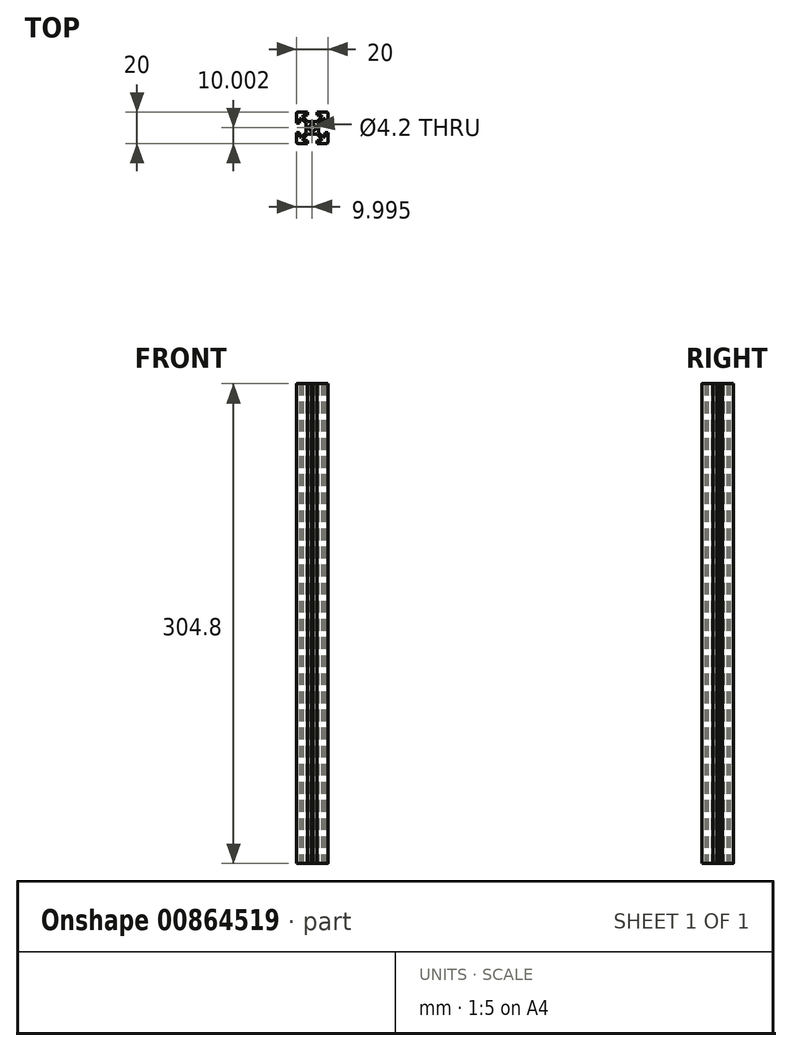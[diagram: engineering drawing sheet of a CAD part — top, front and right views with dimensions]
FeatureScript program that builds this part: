
annotation { "Feature Type Name" : "Feature", "Feature Type Description" : "" }
export const myFeature = defineFeature(function(context is Context, id is Id, definition is map)
    precondition{}
    {
        {
            var Q0;
            Q0=qCreatedBy(makeId("Top.planeOp"),FACE);
            var sketch = newSketch(context, id + "F0", { "sketchPlane" : qUnion([Q0])});
            skLineSegment(sketch, "E0", {"start": v(-2.2, 0) * mm, "end": v(2.2, 0) * mm});
            skLineSegment(sketch, "E1", {"start": v(0, -2.21) * mm, "end": v(0, 2.2) * mm});
            skLineSegment(sketch, "E2", {"start": v(-8, -3) * mm, "end": v(-10, -3) * mm});
            skLineSegment(sketch, "E3", {"start": v(-10, -3) * mm, "end": v(-10, -9) * mm});
            skArc(sketch, "E4", {"start": v(-10, -9) * mm, "mid": v(-9.71, -9.71) * mm, "end": v(-9, -10) * mm});
            skLineSegment(sketch, "E5", {"start": v(-9, -10) * mm, "end": v(-3, -10) * mm});
            skLineSegment(sketch, "E6", {"start": v(-3, -10) * mm, "end": v(-3, -8) * mm});
            skLineSegment(sketch, "E7", {"start": v(-3, -8) * mm, "end": v(-6, -8) * mm});
            skLineSegment(sketch, "E8", {"start": v(-6, -8) * mm, "end": v(-6, -7.07) * mm});
            skLineSegment(sketch, "E9", {"start": v(-6, -7.07) * mm, "end": v(-2.94, -4) * mm});
            skLineSegment(sketch, "E10", {"start": v(-2.94, -4) * mm, "end": v(-0.52, -4) * mm});
            skLineSegment(sketch, "E11", {"start": v(-0.52, -4) * mm, "end": v(0, -3.7) * mm});
            skLineSegment(sketch, "E12", {"start": v(0, -3.7) * mm, "end": v(0.51, -4) * mm});
            skLineSegment(sketch, "E13", {"start": v(0.51, -4) * mm, "end": v(2.93, -4) * mm});
            skLineSegment(sketch, "E14", {"start": v(2.93, -4) * mm, "end": v(6, -7.07) * mm});
            skLineSegment(sketch, "E15", {"start": v(6, -7.07) * mm, "end": v(6, -8) * mm});
            skLineSegment(sketch, "E16", {"start": v(6, -8) * mm, "end": v(3, -8) * mm});
            skLineSegment(sketch, "E17", {"start": v(3, -8) * mm, "end": v(3, -10) * mm});
            skLineSegment(sketch, "E18", {"start": v(3, -10) * mm, "end": v(9, -10) * mm});
            skArc(sketch, "E19", {"start": v(9, -10) * mm, "mid": v(9.7, -9.71) * mm, "end": v(10, -9) * mm});
            skLineSegment(sketch, "E20", {"start": v(10, -9) * mm, "end": v(10, -3) * mm});
            skLineSegment(sketch, "E21", {"start": v(10, -3) * mm, "end": v(8, -3) * mm});
            skLineSegment(sketch, "E22", {"start": v(8, -3) * mm, "end": v(8, -6) * mm});
            skLineSegment(sketch, "E23", {"start": v(8, -6) * mm, "end": v(7.06, -6) * mm});
            skLineSegment(sketch, "E24", {"start": v(7.06, -6) * mm, "end": v(4, -2.95) * mm});
            skLineSegment(sketch, "E25", {"start": v(4, -2.95) * mm, "end": v(4, -0.53) * mm});
            skLineSegment(sketch, "E26", {"start": v(4, -0.53) * mm, "end": v(3.7, 0) * mm});
            skLineSegment(sketch, "E27", {"start": v(3.7, 0) * mm, "end": v(4, 0.51) * mm});
            skLineSegment(sketch, "E28", {"start": v(4, 0.51) * mm, "end": v(4, 2.93) * mm});
            skLineSegment(sketch, "E29", {"start": v(4, 2.93) * mm, "end": v(7.06, 6) * mm});
            skLineSegment(sketch, "E30", {"start": v(7.06, 6) * mm, "end": v(8, 6) * mm});
            skLineSegment(sketch, "E31", {"start": v(8, 6) * mm, "end": v(8, 3) * mm});
            skLineSegment(sketch, "E32", {"start": v(8, 3) * mm, "end": v(10, 3) * mm});
            skLineSegment(sketch, "E33", {"start": v(10, 3) * mm, "end": v(10, 9) * mm});
            skArc(sketch, "E34", {"start": v(10, 9) * mm, "mid": v(9.7, 9.7) * mm, "end": v(9, 10) * mm});
            skLineSegment(sketch, "E35", {"start": v(9, 10) * mm, "end": v(3, 10) * mm});
            skLineSegment(sketch, "E36", {"start": v(3, 10) * mm, "end": v(3, 8) * mm});
            skLineSegment(sketch, "E37", {"start": v(3, 8) * mm, "end": v(6, 8) * mm});
            skLineSegment(sketch, "E38", {"start": v(6, 8) * mm, "end": v(6, 7.05) * mm});
            skLineSegment(sketch, "E39", {"start": v(6, 7.05) * mm, "end": v(2.93, 4) * mm});
            skLineSegment(sketch, "E40", {"start": v(2.93, 4) * mm, "end": v(0.51, 4) * mm});
            skLineSegment(sketch, "E41", {"start": v(0.51, 4) * mm, "end": v(0, 3.7) * mm});
            skLineSegment(sketch, "E42", {"start": v(0, 3.7) * mm, "end": v(-0.52, 4) * mm});
            skLineSegment(sketch, "E43", {"start": v(-0.52, 4) * mm, "end": v(-2.94, 4) * mm});
            skLineSegment(sketch, "E44", {"start": v(-2.94, 4) * mm, "end": v(-6, 7.05) * mm});
            skLineSegment(sketch, "E45", {"start": v(-6, 7.05) * mm, "end": v(-6, 8) * mm});
            skLineSegment(sketch, "E46", {"start": v(-6, 8) * mm, "end": v(-3, 8) * mm});
            skLineSegment(sketch, "E47", {"start": v(-3, 8) * mm, "end": v(-3, 10) * mm});
            skLineSegment(sketch, "E48", {"start": v(-3, 10) * mm, "end": v(-9, 10) * mm});
            skArc(sketch, "E49", {"start": v(-9, 10) * mm, "mid": v(-9.71, 9.7) * mm, "end": v(-10, 9) * mm});
            skLineSegment(sketch, "E50", {"start": v(-10, 9) * mm, "end": v(-10, 3) * mm});
            skLineSegment(sketch, "E51", {"start": v(-10, 3) * mm, "end": v(-8, 3) * mm});
            skLineSegment(sketch, "E52", {"start": v(-8, 3) * mm, "end": v(-8, 6) * mm});
            skLineSegment(sketch, "E53", {"start": v(-8, 6) * mm, "end": v(-7.07, 6) * mm});
            skLineSegment(sketch, "E54", {"start": v(-7.07, 6) * mm, "end": v(-4, 2.93) * mm});
            skLineSegment(sketch, "E55", {"start": v(-4, 2.93) * mm, "end": v(-4, 0.51) * mm});
            skLineSegment(sketch, "E56", {"start": v(-4, 0.51) * mm, "end": v(-3.7, 0) * mm});
            skLineSegment(sketch, "E57", {"start": v(-3.7, 0) * mm, "end": v(-4, -0.53) * mm});
            skLineSegment(sketch, "E58", {"start": v(-4, -0.53) * mm, "end": v(-4, -2.95) * mm});
            skLineSegment(sketch, "E59", {"start": v(-4, -2.95) * mm, "end": v(-7.07, -6) * mm});
            skLineSegment(sketch, "E60", {"start": v(-7.07, -6) * mm, "end": v(-8, -6) * mm});
            skLineSegment(sketch, "E61", {"start": v(-8, -6) * mm, "end": v(-8, -3) * mm});
            skCircle(sketch, "E62", {"center": v(0, 0) * mm, "radius": 2.1 * mm});
            skSolve(sketch);
        }
        {
            var Q0;
            Q0 = qSketchRegion(id + "F0", true);
            extrude(context, id + "F1", {"entities" : qUnion([Q0]), "depth" : 304.8 * mm, "offsetDistance" : 25.4 * mm});
        }
    });
